# Revit family: A132400S-VR
name_source: partatom
category: Plumbing Fixtures
revit_build: Autodesk Revit 2018 (Build: 20170223_1515(x64)
units: mm (PartAtom-declared; Revit-internal decimal feet)

## family parameters
Cut with Voids When Loaded = No
Host = Face
OmniClass Number = 23.65.70.14.11
OmniClass Title = Drinking Fountains/Coolers
Part Type = Normal
Room Calculation Point = No
Round Connector Dimension = Use Diameter
Shared = Yes

## types (6) — shared parameters
AP3 - Access panel for a dual fountain (Must select -MF8) = No
Assembly Code = D2010810
CW Connection = Yes
CWFU = 1.5
Connection Size = 1 1/4"
Default Elevation = 33"
Depth = 18 1/2"
Description = Oval Bowl Barrier-Free, Vandal Resistant, Wall Mount Bi-Level Drinking Fountain with 32 Trim Panel
HP - High polished stainless steel = No
HW Connection = No
Inlet Diameter Connection = 3/8"
Length = 32 1/4"
Manufacturer = Murdock Manufacturing
Model = A132-VR
Product Documentation Link = https://www.murdockmfg.com
Product Page URL = https://www.murdockmfg.com
RBL - Reverse bi-level = No
SK4 - Skirt kit, stainless steel for upper unit = No
URL = https://www.murdockmfg.com
Vent Connection = No
WF1 - 1500 gallon capacity, NSF 42+53, 1 micron lead reduction filter = No
WFU = 2
Warranty Documentation Link = https://www.murdockmfg.com
Waste Connection = Yes
Width = 32"
zero-valued in all types: HWFU

## per-type parameters (varying)
| type | A132200-VR - Bronze finish | A132300 - Gold finish (high polished only) | A132400 - Stainless Steel (Std) | F - Flexible bubbler | Material | S - Lead-Free Stainless Steel bubbler | W32-CSC Concealed support carrier |
| A132200S-VR | Yes | No | No | No | Metal-Murdock-18 Gage-Type 304-Bronze | Yes | Yes |
| A132300F-VR | No | Yes | No | Yes | Metal-Murdock-18 Gage-Type 304-Gold | No | Yes |
| A132400F-VR | No | No | Yes | Yes | Metal-Murdock-18 Gage-Type 304-Stainless Satin | No | No |
| A132300S-VR | No | Yes | No | No | Metal-Murdock-18 Gage-Type 304-Gold | Yes | Yes |
| A132400S-VR | No | No | Yes | No | Metal-Murdock-18 Gage-Type 304-Stainless Satin | Yes | No |
| A132200F-VR | Yes | No | No | Yes | Metal-Murdock-18 Gage-Type 304-Bronze | No | Yes |

## geometry (parser evidence)
native form markers: Sweep x2
no freeform markers — native parametric forms only
